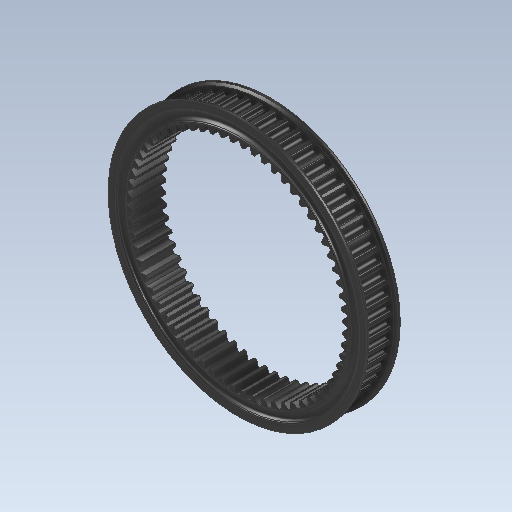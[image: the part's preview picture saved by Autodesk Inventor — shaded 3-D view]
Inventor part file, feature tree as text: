
AUTODESK INVENTOR PART (.ipt)
format: ipt  version: 2020 (Build 240168000, 168)  size: 1,344,000 bytes
history: native  units: mm (DEFAULTED — no unit token found)
features: sketch x5, extrude x4, plane x4, other x3, revolve x2, chamfer x1, mirror x1, fillet x1
ambient origin geometry x8: Origin, YZ Plane, XZ Plane, XY Plane, X Axis, Y Axis, Z Axis, Center Point
bodies: Solid1 (feature_tree)
feature tree (21):
  extrude  "Extrusion1"  Depth=12.7mm TaperAngle=0.0deg
  plane  "Work Plane1"
  plane  "Work Plane2"
  plane  "Work Plane3"
  other  "Spur Gear"
  sketch  "Sketch3"  dims[d6=0.0mm d7=0.490874mm d9=0.0mm]
  extrude  "Extrusion2"  Depth=76.2mm TaperAngle=0.0deg
  extrude  "Extrusion3"  TaperAngle=0.0deg  [1 undecoded]
  extrude  "Extrusion6"  TaperAngle=0.0deg  [1 undecoded]
  plane  "Work Plane4"
  chamfer  "Chamfer1"  Distance=30.48mm
  mirror  "Mirror1"
  sketch  "Sketch6"  dims[d20=94.35mm d21=90.19mm d23=1.047198mm d24=3.05mm d26=600.0mm d28=360.0deg d30=25.4mm d31=0.0mm d32=25.4mm d33=0.0mm d34=0.01mm d35=0.01mm d43=1.5875mm d44=0.0mm d45=3.175mm d46=44.45mm d48=90.0deg d49=0.79375mm d50=3.175mm d51=45.0deg d52=0.9mm d53=98.425mm d54=90.0deg d55=2.794mm d57=0.5mm]
  revolve  "Revolution1"  [1 undecoded]
  revolve  "Revolution2"  [1 undecoded]
  fillet  "Fillet2"  Radius=3.05mm
  sketch  "Sketch1"  dims[d0=92.9005mm d1=12.7mm d2=0.0mm]
  sketch  "Sketch2"  dims[d3=81.28mm d4=76.2mm d5=0.0mm]
  other  "Srf1"
  sketch  "Sketch4"  dims[d14=0.0mm d15=30.48mm d16=0.0mm d17=0.0mm d18=0.0mm d19=30.48mm]
  other  "Pitch Diameter"
note: 4 required parameter values undecoded (feature->parameter linkage not recoverable at this tier; creation-order binding heuristic only, values carry confidence <= 0.55)